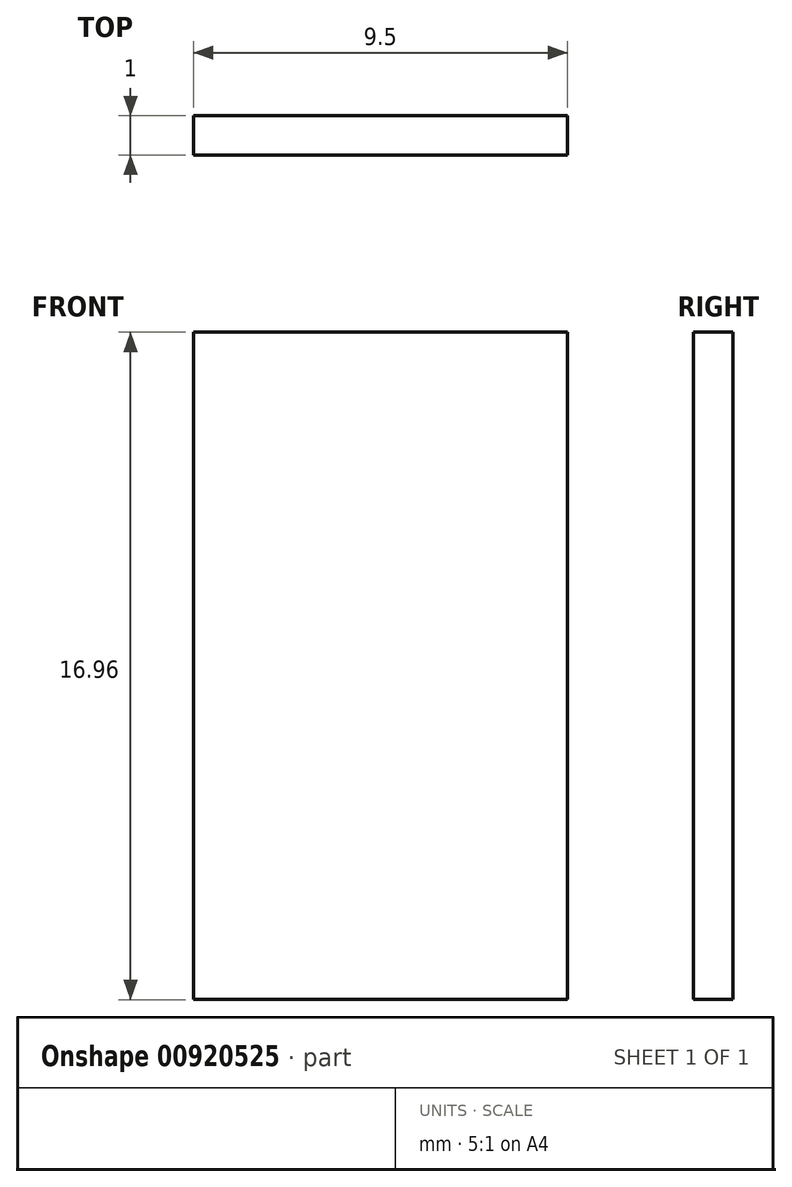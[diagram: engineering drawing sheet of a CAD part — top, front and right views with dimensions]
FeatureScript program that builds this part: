
annotation { "Feature Type Name" : "Feature", "Feature Type Description" : "" }
export const myFeature = defineFeature(function(context is Context, id is Id, definition is map)
    precondition{}
    {
        {
            var Q0;
            Q0=qCreatedBy(makeId("Front.planeOp"),FACE);
            var sketch = newSketch(context, id + "F0", { "sketchPlane" : qUnion([Q0])});
            skLineSegment(sketch, "E0.bottom", {"start": v(4.75, -8.48) * mm, "end": v(-4.75, -8.48) * mm});
            skLineSegment(sketch, "E0.top", {"start": v(4.75, 8.48) * mm, "end": v(-4.75, 8.48) * mm});
            skLineSegment(sketch, "E0.left", {"start": v(4.75, -8.48) * mm, "end": v(4.75, 8.48) * mm});
            skLineSegment(sketch, "E0.right", {"start": v(-4.75, -8.48) * mm, "end": v(-4.75, 8.48) * mm});
            skPoint(sketch, "E0.middle", {"position": v(0, 0) * mm});
            skSolve(sketch);
        }
        {
            var Q0;
            Q0=makeQuery(id+"F0.imprint","IMPRINT",FACE,{"disambiguationData":[TD([[makeQuery(id+"F0.imprint","IMPRINT",EDGE,{"derivedFrom":sQuery(id+"F0.wireOp",EDGE,"E0.bottom")}),-1.0]])]});
            extrude(context, id + "F1", {"entities" : qUnion([Q0]), "depth" : 1 * mm, "offsetDistance" : 25 * mm});
        }
    });
